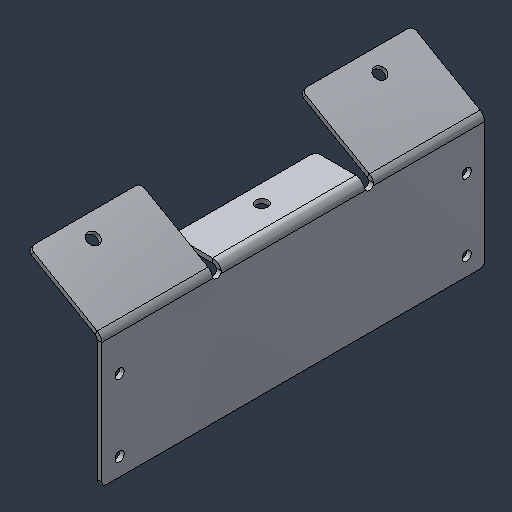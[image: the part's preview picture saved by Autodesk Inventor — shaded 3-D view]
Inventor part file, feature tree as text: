
AUTODESK INVENTOR PART (.ipt)
format: ipt  version: 2024.3 (Build 283343000, 343)  size: 145,408 bytes
history: native  units: mm (DEFAULTED — no unit token found)
features: fillet x1
ambient origin geometry x8: Origin, YZ Plane, XZ Plane, XY Plane, X Axis, Y Axis, Z Axis, Center Point
bodies: Solid1 (feature_tree)
feature tree (1):
  fillet  "Fillet3"  [1 undecoded]
note: 1 required parameter value undecoded (feature->parameter linkage not recoverable at this tier; creation-order binding heuristic only, values carry confidence <= 0.55)
